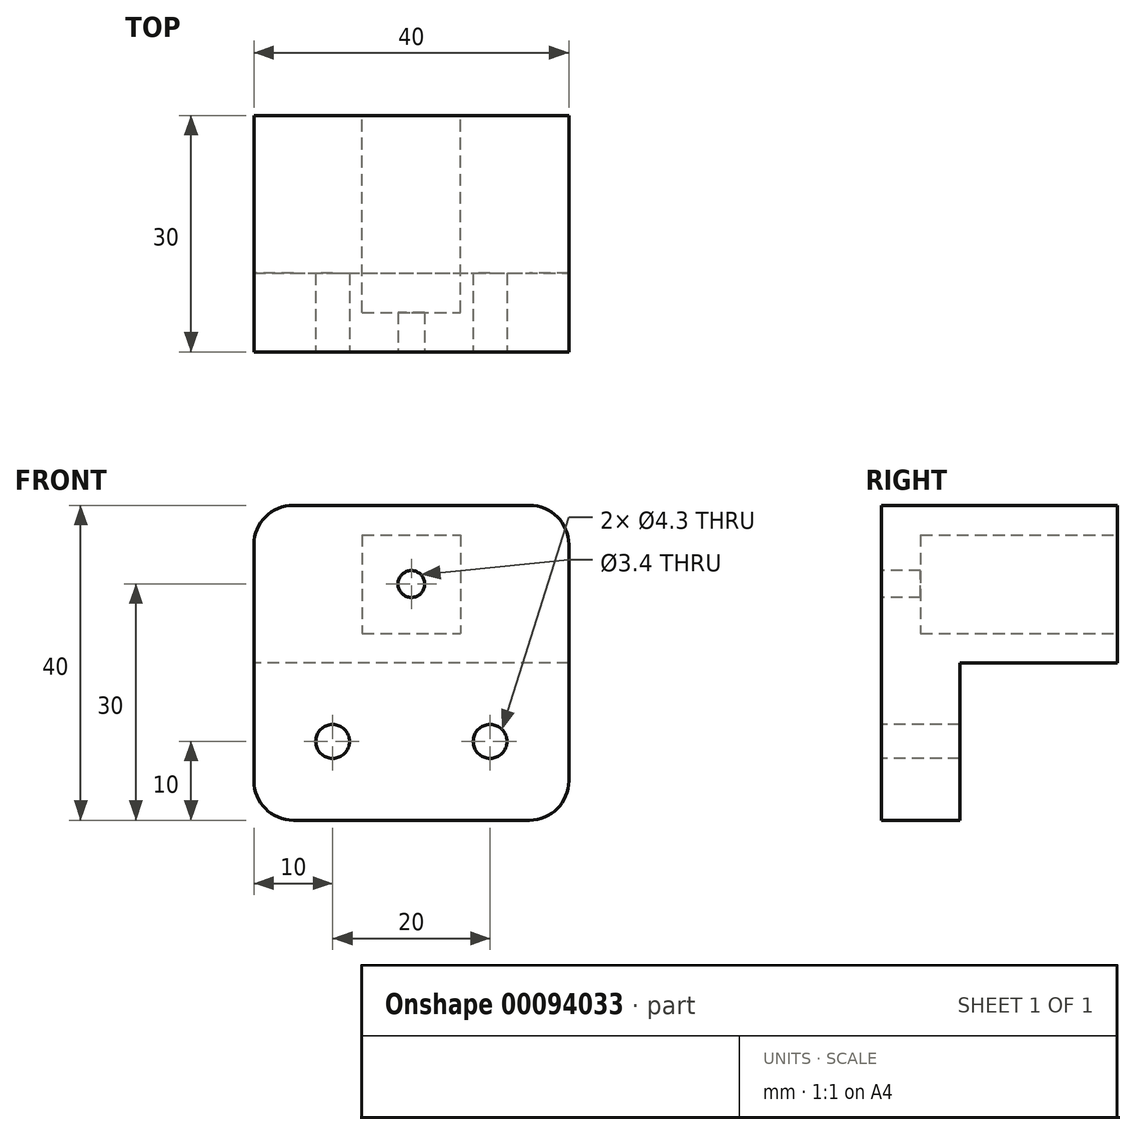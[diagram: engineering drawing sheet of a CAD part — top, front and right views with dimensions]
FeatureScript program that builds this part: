
annotation { "Feature Type Name" : "Feature", "Feature Type Description" : "" }
export const myFeature = defineFeature(function(context is Context, id is Id, definition is map)
    precondition{}
    {
        {
            var Q0;
            Q0=qCreatedBy(makeId("Top.planeOp"),FACE);
            var sketch = newSketch(context, id + "F0", { "sketchPlane" : qUnion([Q0])});
            skLineSegment(sketch, "E0.bottom", {"start": v(20, 15) * mm, "end": v(-20, 15) * mm});
            skLineSegment(sketch, "E0.top", {"start": v(20, -15) * mm, "end": v(-20, -15) * mm});
            skLineSegment(sketch, "E0.left", {"start": v(20, 15) * mm, "end": v(20, -15) * mm});
            skLineSegment(sketch, "E0.right", {"start": v(-20, 15) * mm, "end": v(-20, -15) * mm});
            skPoint(sketch, "E0.middle", {"position": v(0, 0) * mm});
            skLineSegment(sketch, "E1", {"start": v(-20, -5) * mm, "end": v(20, -5) * mm});
            skSolve(sketch);
        }
        {
            var Q0;
            Q0 = qSketchRegion(id + "F0", true);
            extrude(context, id + "F1", {"entities" : qUnion([Q0]), "depth" : 40 * mm});
        }
        {
            var Q0;
            {var subQ0=sQuery(id+"F0.wireOp",EDGE,"E0.bottom");Q0=makeQuery(id+"F0.imprint","IMPRINT",FACE,{"disambiguationData":[TD([[makeQuery(id+"F0.imprint","IMPRINT",EDGE,{"derivedFrom":subQ0}),1.0]])]});}
            extrude(context, id + "F2", {"entities" : qUnion([Q0]), "operationType" : NewBodyOperationType.REMOVE, "depth" : 20 * mm});
        }
        {
            var Q0;
            Q0=makeQuery(id+"F1.opExtrude","SWEPT_FACE",FACE,{"disambiguationData":[OSD([sQuery(id+"F0.wireOp",EDGE,"E0.top")])]});
            var sketch = newSketch(context, id + "F3", { "sketchPlane" : qUnion([Q0])});
            skCircle(sketch, "E2", {"center": v(-10, 10) * mm, "radius": 2.15 * mm});
            skCircle(sketch, "E3", {"center": v(10, 10) * mm, "radius": 2.15 * mm});
            skCircle(sketch, "E4", {"center": v(0, 30) * mm, "radius": 1.7 * mm});
            skSolve(sketch);
        }
        {
            var Q0;
            Q0 = qSketchRegion(id + "F3", true);
            extrude(context, id + "F4", {"entities" : qUnion([Q0]), "operationType" : NewBodyOperationType.REMOVE, "oppositeDirection" : true, "depth" : 40 * mm});
        }
        {
            var Q0;
            Q0=makeQuery(id+"F1.opExtrude","SWEPT_FACE",FACE,{"disambiguationData":[OSD([sQuery(id+"F0.wireOp",EDGE,"E0.bottom")])]});
            var sketch = newSketch(context, id + "F5", { "sketchPlane" : qUnion([Q0])});
            skLineSegment(sketch, "E5.bottom", {"start": v(6.25, 36.25) * mm, "end": v(-6.25, 36.25) * mm});
            skLineSegment(sketch, "E5.top", {"start": v(6.25, 23.75) * mm, "end": v(-6.25, 23.75) * mm});
            skLineSegment(sketch, "E5.left", {"start": v(6.25, 36.25) * mm, "end": v(6.25, 23.75) * mm});
            skLineSegment(sketch, "E5.right", {"start": v(-6.25, 36.25) * mm, "end": v(-6.25, 23.75) * mm});
            skPoint(sketch, "E5.middle", {"position": v(0, 30) * mm});
            skSolve(sketch);
        }
        {
            var Q0;
            Q0=makeQuery(id+"F5.imprint","IMPRINT",FACE,{"disambiguationData":[TD([[makeQuery(id+"F5.imprint","IMPRINT",EDGE,{"derivedFrom":sQuery(id+"F5.wireOp",EDGE,"E5.bottom")}),1.0]])]});
            extrude(context, id + "F6", {"entities" : qUnion([Q0]), "operationType" : NewBodyOperationType.REMOVE, "oppositeDirection" : true, "depth" : 25 * mm});
        }
        {
            var Q0;
            Q0=makeQuery(id+"F1.opExtrude","CAP_EDGE",EDGE,{"disambiguationData":[OSD([sQuery(id+"F0.wireOp",EDGE,"E0.right")])],"isStart":true});
            var Q1;
            Q1=makeQuery(id+"F1.opExtrude","CAP_EDGE",EDGE,{"disambiguationData":[OSD([sQuery(id+"F0.wireOp",EDGE,"E0.left")])],"isStart":true});
            var Q2;
            Q2=makeQuery(id+"F1.opExtrude","CAP_EDGE",EDGE,{"disambiguationData":[OSD([sQuery(id+"F0.wireOp",EDGE,"E0.right")])],"isStart":false});
            var Q3;
            Q3=makeQuery(id+"F1.opExtrude","CAP_EDGE",EDGE,{"disambiguationData":[OSD([sQuery(id+"F0.wireOp",EDGE,"E0.left")])],"isStart":false});
            fillet(context, id + "F7", {"entities" : qUnion([Q0, Q1, Q2, Q3]), "radius" : 5 * mm, "tangentPropagation" : true, "allowEdgeOverflow" : false});
        }
    });
